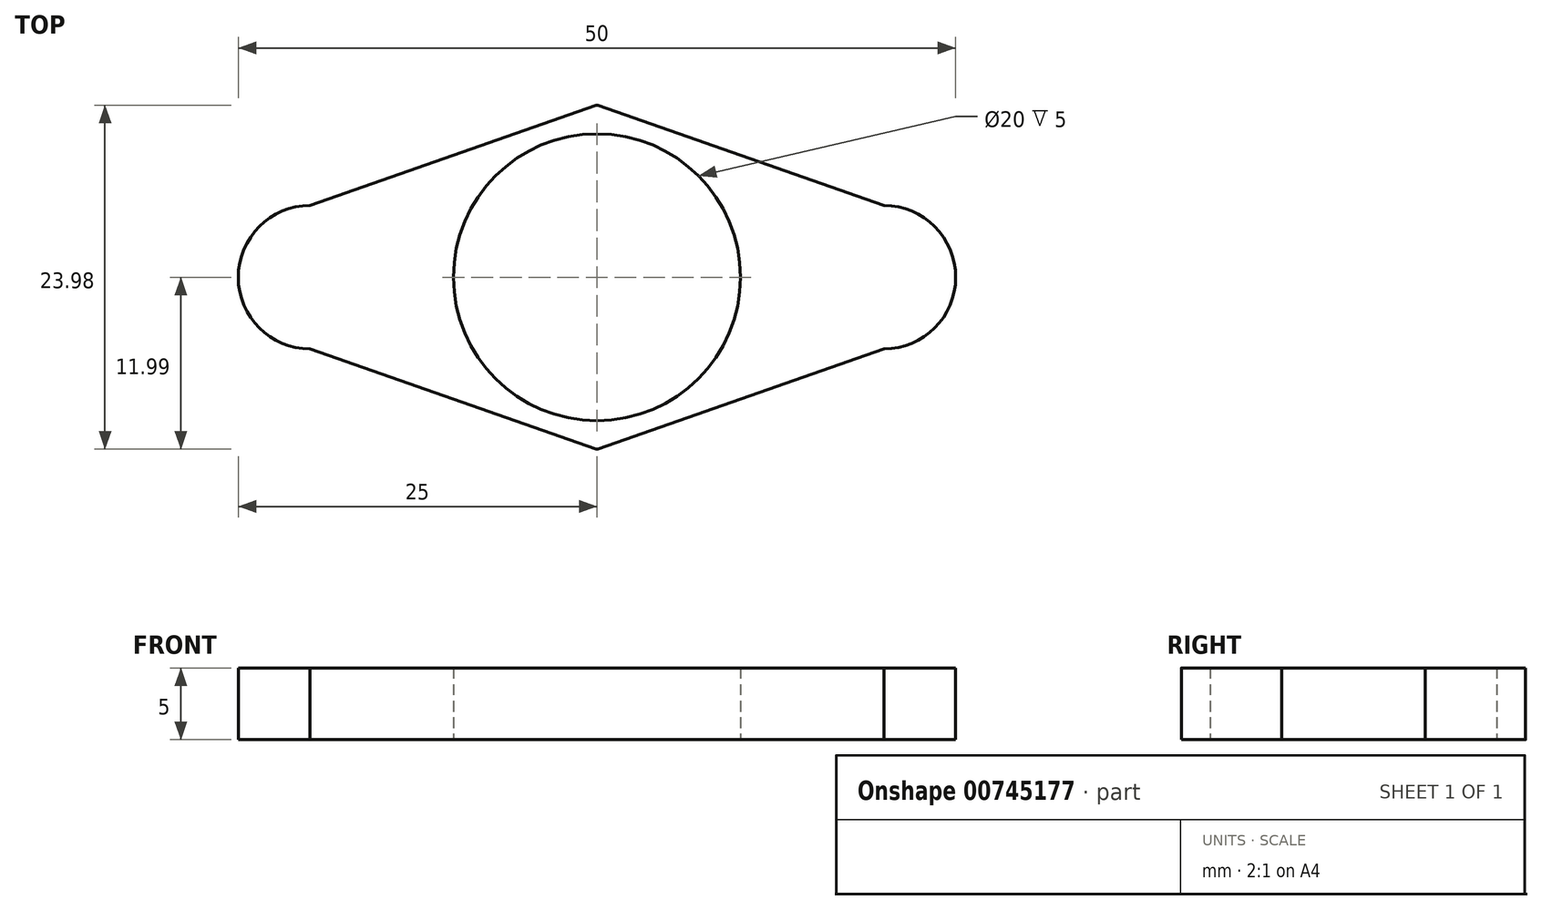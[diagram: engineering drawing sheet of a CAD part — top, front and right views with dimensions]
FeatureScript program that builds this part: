
annotation { "Feature Type Name" : "Feature", "Feature Type Description" : "" }
export const myFeature = defineFeature(function(context is Context, id is Id, definition is map)
    precondition{}
    {
        {
            var Q0;
            Q0=qCreatedBy(makeId("Top.planeOp"),FACE);
            var sketch = newSketch(context, id + "F0", { "sketchPlane" : qUnion([Q0])});
            skArc(sketch, "E0", {"start": v(-20, 5) * mm, "mid": v(-25, 0) * mm, "end": v(-20, -5) * mm});
            skArc(sketch, "E1", {"start": v(20, -5) * mm, "mid": v(25, 0) * mm, "end": v(20, 5) * mm});
            skCircle(sketch, "E2", {"center": v(0, 0) * mm, "radius": 10 * mm});
            skArc(sketch, "E3", {"start": v(7.48, -9.38) * mm, "mid": v(12, 0) * mm, "end": v(7.48, 9.38) * mm});
            skLineSegment(sketch, "E4", {"start": v(-20, 5) * mm, "end": v(-0.07, 11.98) * mm});
            skLineSegment(sketch, "E5", {"start": v(-20, -5) * mm, "end": v(-0.07, -11.98) * mm});
            skLineSegment(sketch, "E6", {"start": v(0.07, -11.98) * mm, "end": v(20, -5) * mm});
            skLineSegment(sketch, "E7", {"start": v(0.07, 11.98) * mm, "end": v(20, 5) * mm});
            skArc(sketch, "E8.trimOffspring", {"start": v(-7.48, 9.38) * mm, "mid": v(-12, 0) * mm, "end": v(-7.48, -9.38) * mm});
            skPoint(sketch, "E9.visualSharp", {"position": v(0, 12) * mm});
            skArc(sketch, "E9.filletArc", {"start": v(0.07, 11.98) * mm, "mid": v(0, 11.99) * mm, "end": v(-0.07, 11.98) * mm});
            skPoint(sketch, "E10.visualSharp", {"position": v(0, -12) * mm});
            skArc(sketch, "E10.filletArc", {"start": v(-0.07, -11.98) * mm, "mid": v(0, -11.99) * mm, "end": v(0.07, -11.98) * mm});
            skSolve(sketch);
        }
        {
            var Q0;
            Q0 = qSketchRegion(id + "F0", true);
            extrude(context, id + "F1", {"entities" : qUnion([Q0]), "depth" : 5 * mm, "offsetDistance" : 25 * mm});
        }
    });
